# Revit family: IS_Ipalyss_E1396_BIM_GB
name_source: partatom
category: Plumbing Fixtures
revit_build: Autodesk Revit 2017 (Build: 20160225_1515(x64)
units: mm (PartAtom-declared; Revit-internal decimal feet)

## family parameters
Always vertical = No
Cut with Voids When Loaded = No
OmniClass Number = 23.45.05.14.14
OmniClass Title = Sinks/Lavatories
Part Type = Normal
Room Calculation Point = No
Round Connector Dimension = Use Diameter
Shared = No
Work Plane-Based = No

## types (1)
- E139601 - IPALYSS VSL BSN 60X38 WHITE OVAL NOF NTH
    Accessories = www.idealspec.co.uk
    AreaUnits = millimeters
    AssetType = Fixed
    BIMObjectName = IS_IdealStandard_CounterTopWashBasins_IPALYSS_E1396
    BarCode = 5017830545934
    Brand = Ideal Standard
    Category = SanitaryTerminal_WASHHANDBASIN_UK
    CodePerformance = 6
    Color = White
    ConnectionType = Plumbing
    Description = E139601  IPALYSS VSL BSN 60X38 WHITE OVAL NOF NTH
    DurationUnit = year
    ExpectedLife = 99
    Features = Washbasin 60X38 WHITE OVAL NOF NTH
    Finish = White
    IfcExportAs = IfcSanitaryTerminalType
    IfcExportType = WASHHANDBASIN
    Installation instructions = http://www.idealspec.co.uk
    InstallationInstructions = www.idealspec.co.uk/resources.html
    LinearUnits = millimeters
    MainColor = white
    ManufacturerURL = www.idealspec.co.uk
    Material = Ceramic
    Model = E139601
    ModelNumber = E139601
    ModelReference = IPALYSS Counter Top Wash Basins
    Name = CounterTopWashBasins_IPALYSS_E1396_IdealStandard
    NettWeight = 9 Kg
    NominalDepth = 375 mm
    NominalHeight = 120 mm
    NominalLength = 390 mm  [stored 1.27953 ft]
    NominalWidth = 600 mm
    Product group = Basin
    ProductInformation = www.idealspec.co.uk/assets/datasheet/E139601
    Shape = Sculptured
    Size = 375 x 120 x 600mm
    SpareParts = www.fastpart-spares.co.uk
    URL = www.idealspec.co.uk
    Uniclass 2015 Code = Pr_40_20_96_18
    Uniclass 2015 Name = Counter top wash basins
    Uniclass2015Code = Pr_40_20_96_18
    Uniclass2015Title = Counter top wash basins
    Uniclass2015Version = Products v1.15
    Version = 1
    VolumeUnits = Litres
    WarrantyDescription = Manufacturers warranty
    WarrantyDurationParts = 99
    WarrantyDurationUnit = year
    WashHandBasinMounting = Counter top
    WashHandBasinType = HandRinse

note: [stored X ft] marks values corroborated as IEEE doubles in the binary element streams (Revit-internal decimal feet)

## geometry (parser evidence)
native form markers: Sweep x4
no freeform markers — native parametric forms only
